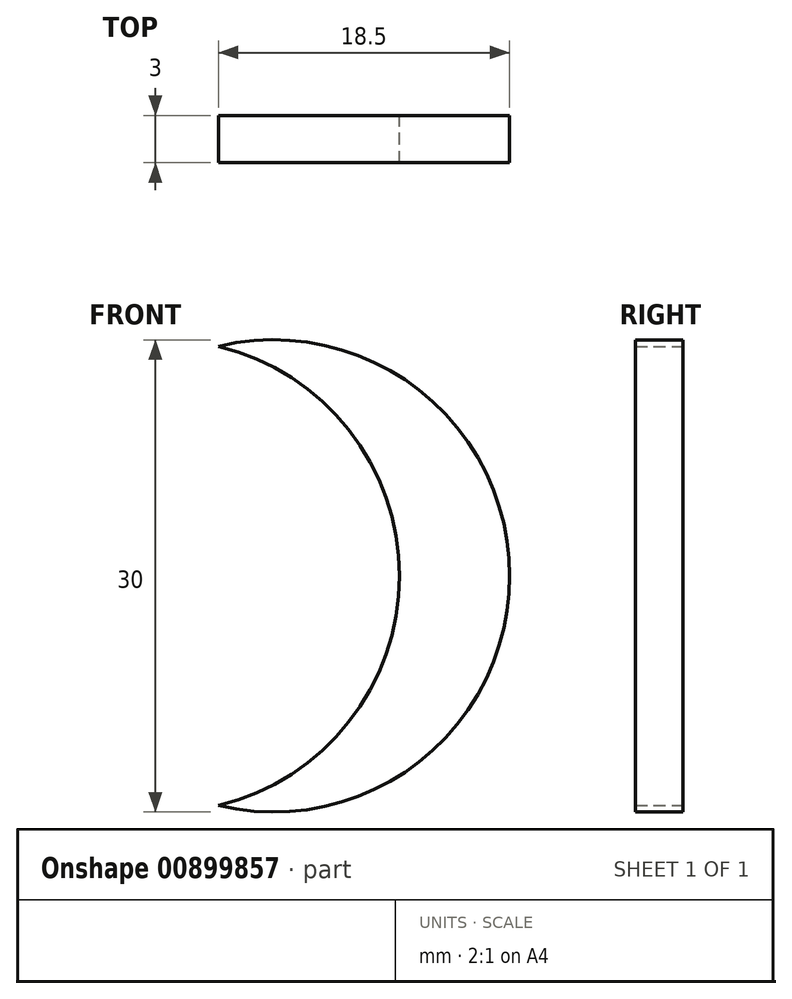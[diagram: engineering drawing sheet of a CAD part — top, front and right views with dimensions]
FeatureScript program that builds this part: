
annotation { "Feature Type Name" : "Feature", "Feature Type Description" : "" }
export const myFeature = defineFeature(function(context is Context, id is Id, definition is map)
    precondition{}
    {
        {
            var Q0;
            Q0=qCreatedBy(makeId("Front.planeOp"),FACE);
            var sketch = newSketch(context, id + "F0", { "sketchPlane" : qUnion([Q0])});
            skArc(sketch, "E0", {"start": v(-3.5, -14.59) * mm, "mid": v(15, 0) * mm, "end": v(-3.5, 14.59) * mm});
            skArc(sketch, "E1", {"start": v(-3.5, -14.59) * mm, "mid": v(8, 0) * mm, "end": v(-3.5, 14.59) * mm});
            skSolve(sketch);
        }
        {
            var Q0;
            Q0=makeQuery(id+"F0.imprint","IMPRINT",FACE,{"disambiguationData":[TD([[makeQuery(id+"F0.imprint","IMPRINT",EDGE,{"derivedFrom":sQuery(id+"F0.wireOp",EDGE,"E0")}),1.0]])]});
            extrude(context, id + "F1", {"entities" : qUnion([Q0]), "depth" : 3 * mm, "offsetDistance" : 25 * mm});
        }
    });
